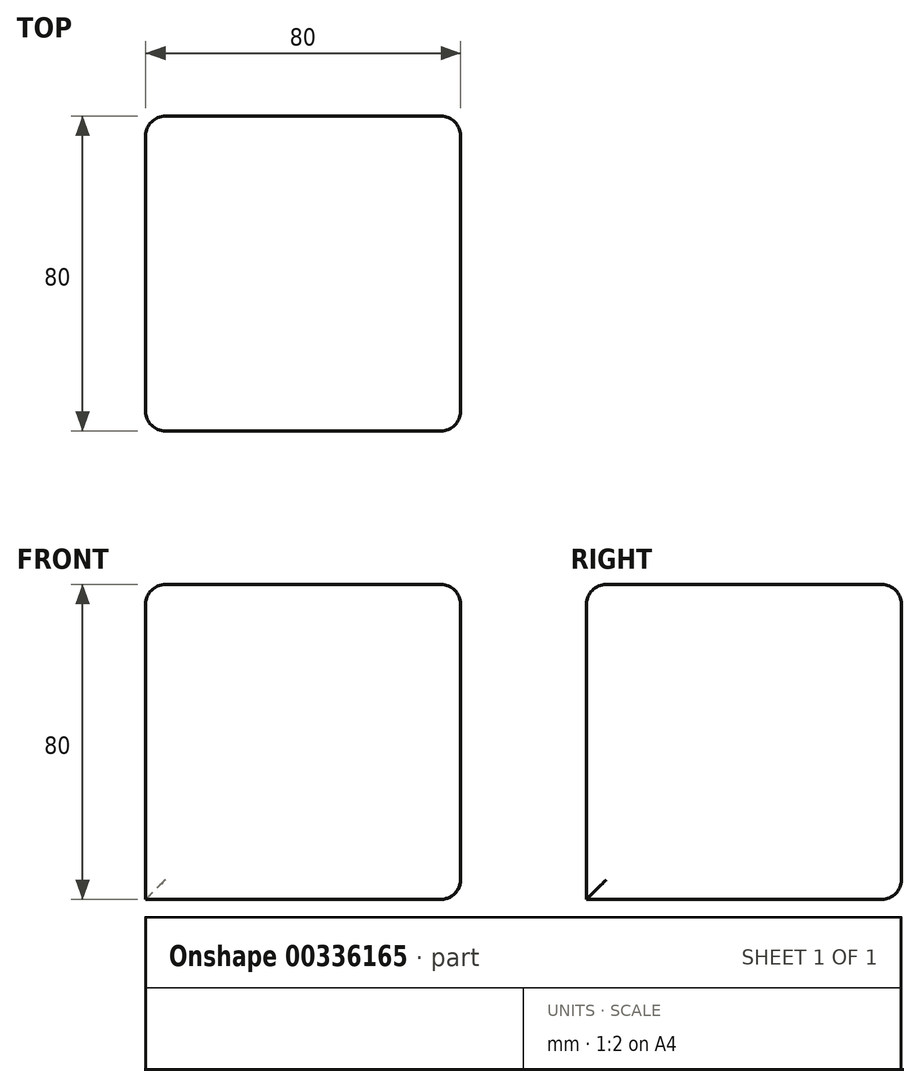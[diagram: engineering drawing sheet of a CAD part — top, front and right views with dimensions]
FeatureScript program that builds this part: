
annotation { "Feature Type Name" : "Feature", "Feature Type Description" : "" }
export const myFeature = defineFeature(function(context is Context, id is Id, definition is map)
    precondition{}
    {
        {
            var Q0;
            Q0=qCreatedBy(makeId("Top.planeOp"),FACE);
            var sketch = newSketch(context, id + "F0", { "sketchPlane" : qUnion([Q0])});
            skLineSegment(sketch, "E0.bottom", {"start": v(-40, 40) * mm, "end": v(40, 40) * mm});
            skLineSegment(sketch, "E0.top", {"start": v(-40, -40) * mm, "end": v(40, -40) * mm});
            skLineSegment(sketch, "E0.left", {"start": v(-40, 40) * mm, "end": v(-40, -40) * mm});
            skLineSegment(sketch, "E0.right", {"start": v(40, 40) * mm, "end": v(40, -40) * mm});
            skPoint(sketch, "E0.middle", {"position": v(0, 0) * mm});
            skSolve(sketch);
        }
        {
            var Q0;
            Q0=makeQuery(id+"F0.imprint","IMPRINT",FACE,{"disambiguationData":[TD([[makeQuery(id+"F0.imprint","IMPRINT",EDGE,{"derivedFrom":sQuery(id+"F0.wireOp",EDGE,"E0.bottom")}),-1.0]])]});
            extrude(context, id + "F1", {"entities" : qUnion([Q0]), "endBound" : BoundingType.SYMMETRIC, "depth" : 80 * mm});
        }
        {
            var Q0;
            Q0=makeQuery(id+"F1.opExtrude","CAP_EDGE",EDGE,{"disambiguationData":[OSD([sQuery(id+"F0.wireOp",EDGE,"E0.top")])],"isStart":false});
            var Q1;
            Q1=makeQuery(id+"F1.opExtrude","CAP_FACE",FACE,{"disambiguationData":[OSD([sQuery(id+"F0.wireOp",EDGE,"E0.bottom"),sQuery(id+"F0.wireOp",EDGE,"E0.top"),sQuery(id+"F0.wireOp",EDGE,"E0.left"),sQuery(id+"F0.wireOp",EDGE,"E0.right")])],"isStart":false});
            var Q2;
            Q2=makeQuery(id+"F1.opExtrude","SWEPT_FACE",FACE,{"disambiguationData":[OSD([sQuery(id+"F0.wireOp",EDGE,"E0.right")])]});
            var Q3;
            Q3=makeQuery(id+"F1.opExtrude","SWEPT_FACE",FACE,{"disambiguationData":[OSD([sQuery(id+"F0.wireOp",EDGE,"E0.bottom")])]});
            var Q4;
            Q4=makeQuery(id+"F1.opExtrude","SWEPT_EDGE",EDGE,{"disambiguationData":[OSD([sQuery(id+"F0.wireOp",EDGE,"E0.top"),sQuery(id+"F0.wireOp",EDGE,"E0.left")])]});
            fillet(context, id + "F2", {"entities" : qUnion([Q0, Q1, Q2, Q3, Q4]), "radius" : 5 * mm, "tangentPropagation" : true, "allowEdgeOverflow" : false});
        }
    });
